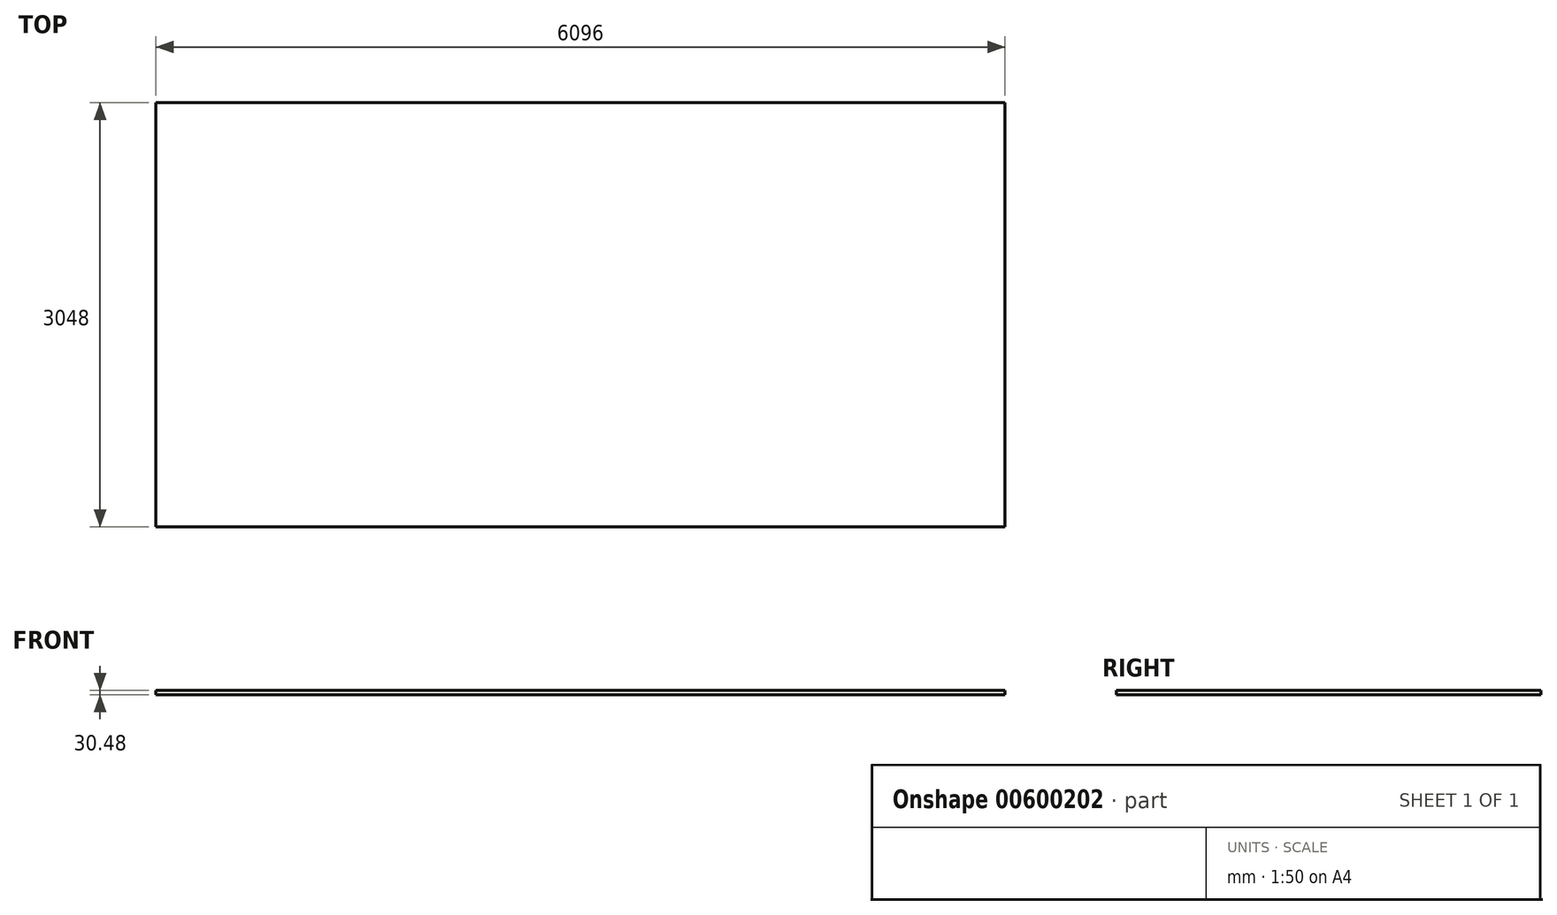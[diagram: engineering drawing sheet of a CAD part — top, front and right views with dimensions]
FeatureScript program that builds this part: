
annotation { "Feature Type Name" : "Feature", "Feature Type Description" : "" }
export const myFeature = defineFeature(function(context is Context, id is Id, definition is map)
    precondition{}
    {
        {
            var Q0;
            Q0=qCreatedBy(makeId("Front.planeOp"),FACE);
            var sketch = newSketch(context, id + "F0", { "sketchPlane" : qUnion([Q0])});
            skLineSegment(sketch, "E0.bottom", {"start": v(-2941.87, 0) * mm, "end": v(3154.13, 0) * mm});
            skLineSegment(sketch, "E0.top", {"start": v(-2941.87, 30.48) * mm, "end": v(3154.13, 30.48) * mm});
            skLineSegment(sketch, "E0.left", {"start": v(-2941.87, 0) * mm, "end": v(-2941.87, 30.48) * mm});
            skLineSegment(sketch, "E0.right", {"start": v(3154.13, 0) * mm, "end": v(3154.13, 30.48) * mm});
            skSolve(sketch);
        }
        {
            var Q0;
            Q0 = qSketchRegion(id + "F0", true);
            extrude(context, id + "F1", {"entities" : qUnion([Q0]), "depth" : 3048 * mm, "offsetDistance" : 30.48 * mm});
        }
    });
